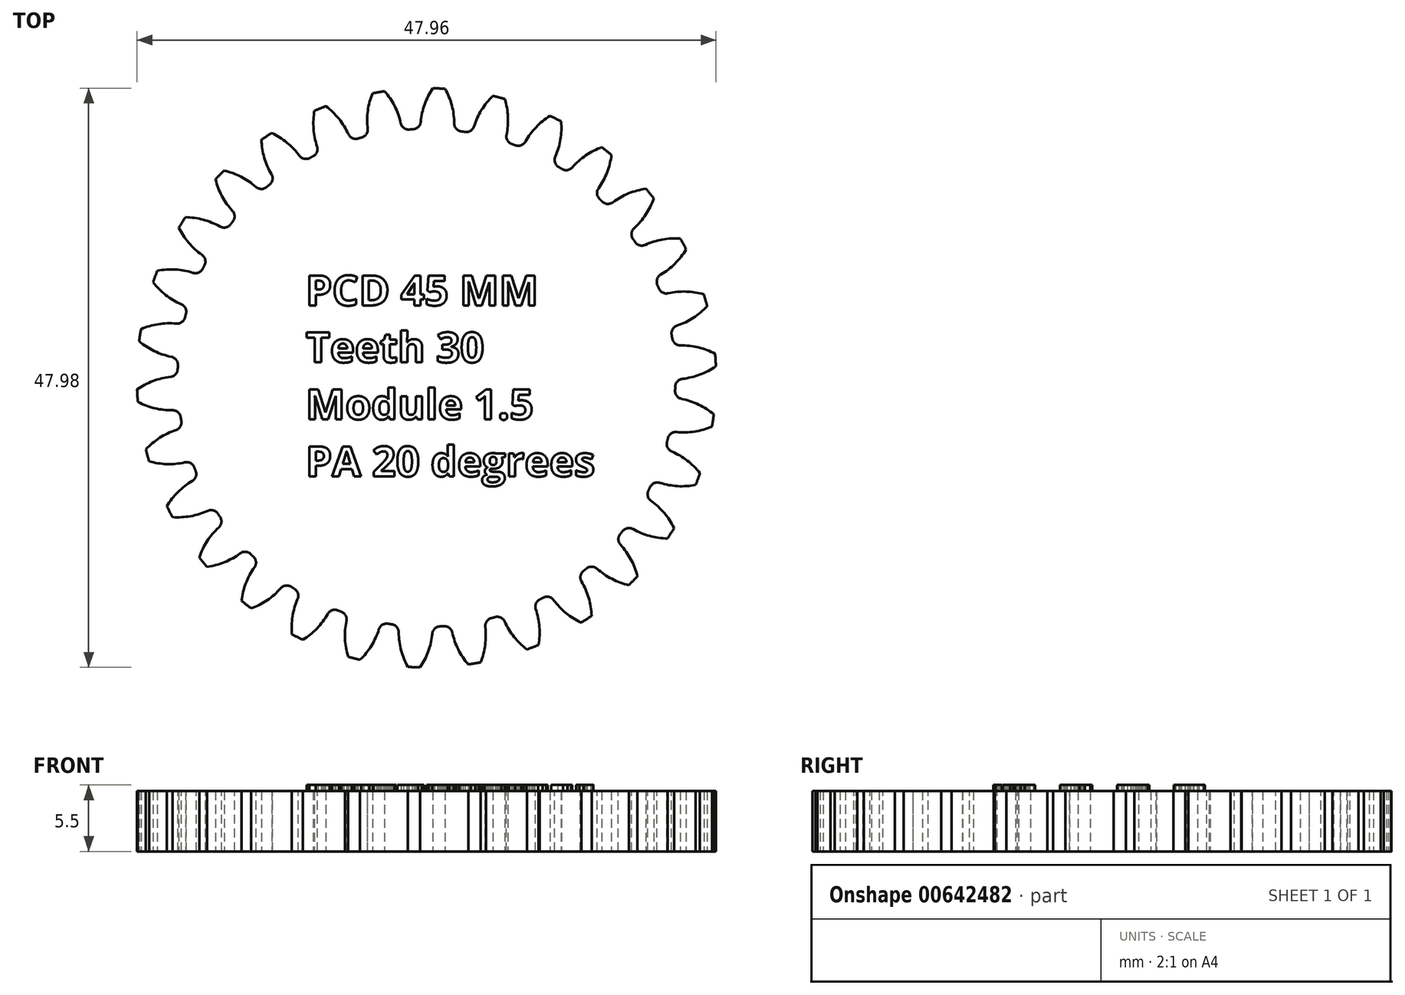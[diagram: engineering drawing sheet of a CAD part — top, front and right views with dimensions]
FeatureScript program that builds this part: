
annotation { "Feature Type Name" : "Feature", "Feature Type Description" : "" }
export const myFeature = defineFeature(function(context is Context, id is Id, definition is map)
    precondition{}
    {
        {
            var Q0;
            Q0=qCreatedBy(makeId("Top.planeOp"),FACE);
            var sketch = newSketch(context, id + "F0", { "sketchPlane" : qUnion([Q0])});
            skCircle(sketch, "E0", {"center": v(0, 0) * mm, "radius": 22.5 * mm, "construction": true});
            skCircle(sketch, "E1", {"center": v(0, 0) * mm, "radius": 20.62 * mm});
            skLineSegment(sketch, "E2", {"start": v(0, 0) * mm, "end": v(0, 40.81) * mm, "construction": true});
            skLineSegment(sketch, "E3", {"start": v(0, 22.5) * mm, "end": v(24.29, 22.5) * mm, "construction": true});
            skLineSegment(sketch, "E4", {"start": v(0, 22.5) * mm, "end": v(24.29, 13.66) * mm, "construction": true});
            skLineSegment(sketch, "E5", {"start": v(0, 0) * mm, "end": v(7.23, 19.87) * mm, "construction": true});
            skCircle(sketch, "E6", {"center": v(0, 0) * mm, "radius": 21.14 * mm, "construction": true});
            skPoint(sketch, "E7", {"position": v(0, 21.14) * mm});
            skPoint(sketch, "E8", {"position": v(0, 24) * mm});
            skPoint(sketch, "E9", {"position": v(0, 23.05) * mm});
            skLineSegment(sketch, "E10", {"start": v(0, 23.05) * mm, "end": v(7.23, 19.87) * mm, "construction": true});
            skPoint(sketch, "E11", {"position": v(5.42, 20.66) * mm});
            skArc(sketch, "E12", {"start": v(-0.5, 20.62) * mm, "mid": v(11.1, 18.94) * mm, "end": v(0.52, 24) * mm, "construction": true});
            skArc(sketch, "E13", {"start": v(0.52, 24) * mm, "mid": v(-0.25, 22.38) * mm, "end": v(-0.5, 20.62) * mm});
            skPoint(sketch, "E14", {"position": v(-0.2, 22.5) * mm});
            skPoint(sketch, "E15", {"position": v(0.97, 22.48) * mm});
            skLineSegment(sketch, "E16", {"start": v(0.97, 22.48) * mm, "end": v(0, 0) * mm, "construction": true});
            skArc(sketch, "E17.MirrorCS", {"start": v(1.54, 23.95) * mm, "mid": v(2.17, 22.28) * mm, "end": v(2.27, 20.5) * mm});
            skArc(sketch, "E18", {"start": v(0.52, 24) * mm, "mid": v(-1.03, -23.98) * mm, "end": v(1.54, 23.95) * mm, "construction": true});
            skArc(sketch, "E19", {"start": v(1.54, 23.95) * mm, "mid": v(1.03, 23.98) * mm, "end": v(0.52, 24) * mm});
            skSolve(sketch);
        }
        {
            var Q0;
            Q0 = qSketchRegion(id + "F0", true);
            extrude(context, id + "F1", {"entities" : qUnion([Q0]), "depth" : 5 * mm, "offsetDistance" : 25 * mm});
        }
        {
            var Q0;
            Q0=makeQuery(id+"F1.opExtrude","SWEPT_EDGE",EDGE,{"disambiguationData":[OSD([sQuery(id+"F0.wireOp",EDGE,"E1"),sQuery(id+"F0.wireOp",EDGE,"E13")])]});
            var Q1;
            Q1=makeQuery(id+"F1.opExtrude","SWEPT_EDGE",EDGE,{"disambiguationData":[OSD([sQuery(id+"F0.wireOp",EDGE,"E1"),sQuery(id+"F0.wireOp",EDGE,"E17.MirrorCS")])]});
            fillet(context, id + "F2", {"entities" : qUnion([Q0, Q1]), "radius" : 0.67 * mm, "tangentPropagation" : true, "allowEdgeOverflow" : false});
        }
        {
            var Q0;
            Q0=makeQuery(id+"F1.opExtrude","SWEPT_BODY",BODY,{"disambiguationData":[OSD([sQuery(id+"F0.wireOp",EDGE,"E1"),sQuery(id+"F0.wireOp",EDGE,"E13"),sQuery(id+"F0.wireOp",EDGE,"E17.MirrorCS"),sQuery(id+"F0.wireOp",EDGE,"E19")])]});
            var Q1;
            Q1=makeQuery(id+"F1.opExtrude","SWEPT_FACE",FACE,{"disambiguationData":[OSD([sQuery(id+"F0.wireOp",EDGE,"E1")])]});
            circularPattern(context, id + "F3", {"operationType" : NewBodyOperationType.ADD, "entities" : qUnion([Q0]), "axis" : qUnion([Q1]), "angle" : 360 * degree, "instanceCount" : 30, "equalSpace" : true});
        }
        {
            var Q0;
            {var subQ0=makeQuery(id+"F1.opExtrude","CAP_FACE",FACE,{"disambiguationData":[OSD([sQuery(id+"F0.wireOp",EDGE,"E1"),sQuery(id+"F0.wireOp",EDGE,"E13"),sQuery(id+"F0.wireOp",EDGE,"E17.MirrorCS"),sQuery(id+"F0.wireOp",EDGE,"E19")])],"isStart":false});Q0=makeQuery(id+"F3.boolean.opBoolean","MERGE",FACE,{"derivedFrom":[subQ0,makeQuery(id+"F3.opPattern","COPY",FACE,{"derivedFrom":subQ0,"instanceName":"1"}),makeQuery(id+"F3.opPattern","COPY",FACE,{"derivedFrom":subQ0,"instanceName":"2"}),makeQuery(id+"F3.opPattern","COPY",FACE,{"derivedFrom":subQ0,"instanceName":"3"}),makeQuery(id+"F3.opPattern","COPY",FACE,{"derivedFrom":subQ0,"instanceName":"4"}),makeQuery(id+"F3.opPattern","COPY",FACE,{"derivedFrom":subQ0,"instanceName":"5"}),makeQuery(id+"F3.opPattern","COPY",FACE,{"derivedFrom":subQ0,"instanceName":"6"}),makeQuery(id+"F3.opPattern","COPY",FACE,{"derivedFrom":subQ0,"instanceName":"7"}),makeQuery(id+"F3.opPattern","COPY",FACE,{"derivedFrom":subQ0,"instanceName":"8"}),makeQuery(id+"F3.opPattern","COPY",FACE,{"derivedFrom":subQ0,"instanceName":"9"}),makeQuery(id+"F3.opPattern","COPY",FACE,{"derivedFrom":subQ0,"instanceName":"10"}),makeQuery(id+"F3.opPattern","COPY",FACE,{"derivedFrom":subQ0,"instanceName":"11"}),makeQuery(id+"F3.opPattern","COPY",FACE,{"derivedFrom":subQ0,"instanceName":"12"}),makeQuery(id+"F3.opPattern","COPY",FACE,{"derivedFrom":subQ0,"instanceName":"13"}),makeQuery(id+"F3.opPattern","COPY",FACE,{"derivedFrom":subQ0,"instanceName":"14"}),makeQuery(id+"F3.opPattern","COPY",FACE,{"derivedFrom":subQ0,"instanceName":"15"}),makeQuery(id+"F3.opPattern","COPY",FACE,{"derivedFrom":subQ0,"instanceName":"16"}),makeQuery(id+"F3.opPattern","COPY",FACE,{"derivedFrom":subQ0,"instanceName":"17"}),makeQuery(id+"F3.opPattern","COPY",FACE,{"derivedFrom":subQ0,"instanceName":"18"}),makeQuery(id+"F3.opPattern","COPY",FACE,{"derivedFrom":subQ0,"instanceName":"19"}),makeQuery(id+"F3.opPattern","COPY",FACE,{"derivedFrom":subQ0,"instanceName":"20"}),makeQuery(id+"F3.opPattern","COPY",FACE,{"derivedFrom":subQ0,"instanceName":"21"}),makeQuery(id+"F3.opPattern","COPY",FACE,{"derivedFrom":subQ0,"instanceName":"22"}),makeQuery(id+"F3.opPattern","COPY",FACE,{"derivedFrom":subQ0,"instanceName":"23"}),makeQuery(id+"F3.opPattern","COPY",FACE,{"derivedFrom":subQ0,"instanceName":"24"}),makeQuery(id+"F3.opPattern","COPY",FACE,{"derivedFrom":subQ0,"instanceName":"25"}),makeQuery(id+"F3.opPattern","COPY",FACE,{"derivedFrom":subQ0,"instanceName":"26"}),makeQuery(id+"F3.opPattern","COPY",FACE,{"derivedFrom":subQ0,"instanceName":"27"}),makeQuery(id+"F3.opPattern","COPY",FACE,{"derivedFrom":subQ0,"instanceName":"28"}),makeQuery(id+"F3.opPattern","COPY",FACE,{"derivedFrom":subQ0,"instanceName":"29"})]});}
            var sketch = newSketch(context, id + "F4", { "sketchPlane" : qUnion([Q0])});
            skText(sketch, "E20", { "text": "PCD 45 MM\nTeeth 30 \nModule 1.5\nPA 20 degrees ", "fontName": "OpenSans-Bold.ttf"});
            const initialGuessF4  = {"E20": [-0.01, 0.006, 1, 0, 0.0025]};
            skSetInitialGuess(sketch, initialGuessF4);
            skSolve(sketch);
        }
        {
            var Q0;
            Q0 = qSketchRegion(id + "F4", true);
            extrude(context, id + "F5", {"entities" : qUnion([Q0]), "operationType" : NewBodyOperationType.ADD, "depth" : 0.5 * mm, "offsetDistance" : 25 * mm});
        }
    });
